# Revit family: NAGARE_STRAIGHT-100
name_source: partatom
category: Site
units: mm (PartAtom-declared; Revit-internal decimal feet)

## family parameters
Always vertical = Yes
Cut with Voids When Loaded = No
Part Type = Normal
Round Connector Dimension = Use Diameter
Shared = Yes
Work Plane-Based = Yes

## types (9) — shared parameters
Manufacturer = www.nagareconcrete.com
URL = https://www.nagareconcrete.com
materiaal_model = NAGARE_FME_(9-).f2_BETON_SI_BERSnl
model_breedte = 1000 mm  [stored 3.28084 ft]
offset_10 = 10 mm  [stored 0.0328084 ft]
offset_voet = 20 mm  [stored 0.0656168 ft]
zichtbaar_voet_extra = No
zero-valued in all types: Default Elevation

## per-type parameters (varying)
| type | beugelpositie_hoogte | model_hoogte | oksel_maatvoering_breedte | oksel_maatvoering_hoogte | voet_hoogte | voet_lengte | voet_type2_150 | voet_type2_base-breedte | voet_type2_hoogte | zichtbaar_voet_type1 | zichtbaar_voet_type2 |
| LP50/100 | 275 mm | 500 mm  [stored 1.64042 ft] | 20 mm  [stored 0.0656168 ft] | 20 mm  [stored 0.0656168 ft] | 120 mm  [stored 0.393701 ft] | 400 mm  [stored 1.31234 ft] | No | 55 mm | 600 mm | Yes | No |
| LP100/100 | 500 mm  [stored 1.64042 ft] | 1000 mm  [stored 3.28084 ft] | 60 mm  [stored 0.19685 ft] | 60 mm  [stored 0.19685 ft] | 120 mm  [stored 0.393701 ft] | 600 mm | No | 55 mm | 600 mm | Yes | No |
| LP125/100 | 625 mm | 1250 mm | 90 mm | 90 mm | 120 mm  [stored 0.393701 ft] | 750 mm | No | 55 mm | 600 mm | Yes | No |
| LP150/100 | 750 mm | 1500 mm | 90 mm | 90 mm | 120 mm  [stored 0.393701 ft] | 850 mm | No | 55 mm | 600 mm | Yes | No |
| LP175/100 | 875 mm | 1750 mm | 125 mm | 125 mm | 120 mm  [stored 0.393701 ft] | 1100 mm | No | 55 mm | 600 mm | No | Yes |
| LP200/100 | 1000 mm  [stored 3.28084 ft] | 2000 mm  [stored 6.56168 ft] | 125 mm | 125 mm | 120 mm  [stored 0.393701 ft] | 1100 mm | No | 55 mm | 600 mm | Yes | No |
| LP225/100 | 1125 mm | 2250 mm | 280 mm | 280 mm | 150 mm | 1350 mm | Yes | 30 mm  [stored 0.0984252 ft] | 600 mm | No | Yes |
| LP250/100 | 1250 mm | 2500 mm | 280 mm | 310 mm | 150 mm | 1350 mm | Yes | 55 mm | 800 mm | No | Yes |
| LP75/100 | 375 mm | 750 mm | 20 mm  [stored 0.0656168 ft] | 20 mm  [stored 0.0656168 ft] | 120 mm  [stored 0.393701 ft] | 500 mm  [stored 1.64042 ft] | No | 55 mm | 600 mm | Yes | No |

note: column(s) folded — value = type name in every type: Type Comments

note: [stored X ft] marks values corroborated as IEEE doubles in the binary element streams (Revit-internal decimal feet)

## geometry (parser evidence)
native form markers: Sweep x3
no freeform markers — native parametric forms only
